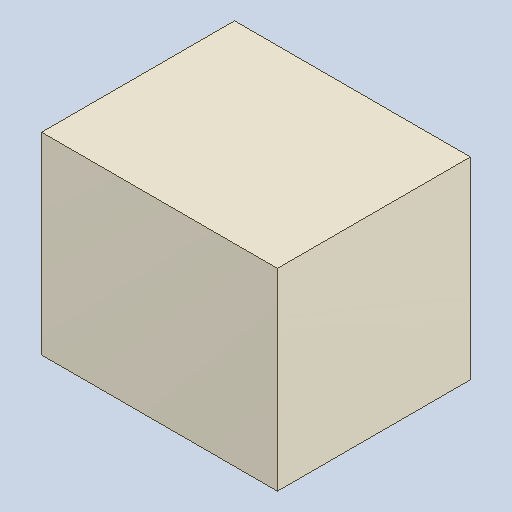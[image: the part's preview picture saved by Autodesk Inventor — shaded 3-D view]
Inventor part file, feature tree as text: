
AUTODESK INVENTOR PART (.ipt)
format: ipt  version: 2023.4 (Build 274418000, 418)  size: 81,920 bytes
history: native  units: mm
features: extrude x1
ambient origin geometry x8: Origin, YZ Plane, XZ Plane, XY Plane, X Axis, Y Axis, Z Axis, Center Point
bodies: Solid1 (feature_tree)
feature tree (1):
  extrude  "Extruded_11"  [1 undecoded]
note: 1 required parameter value undecoded (feature->parameter linkage not recoverable at this tier; creation-order binding heuristic only, values carry confidence <= 0.55)
